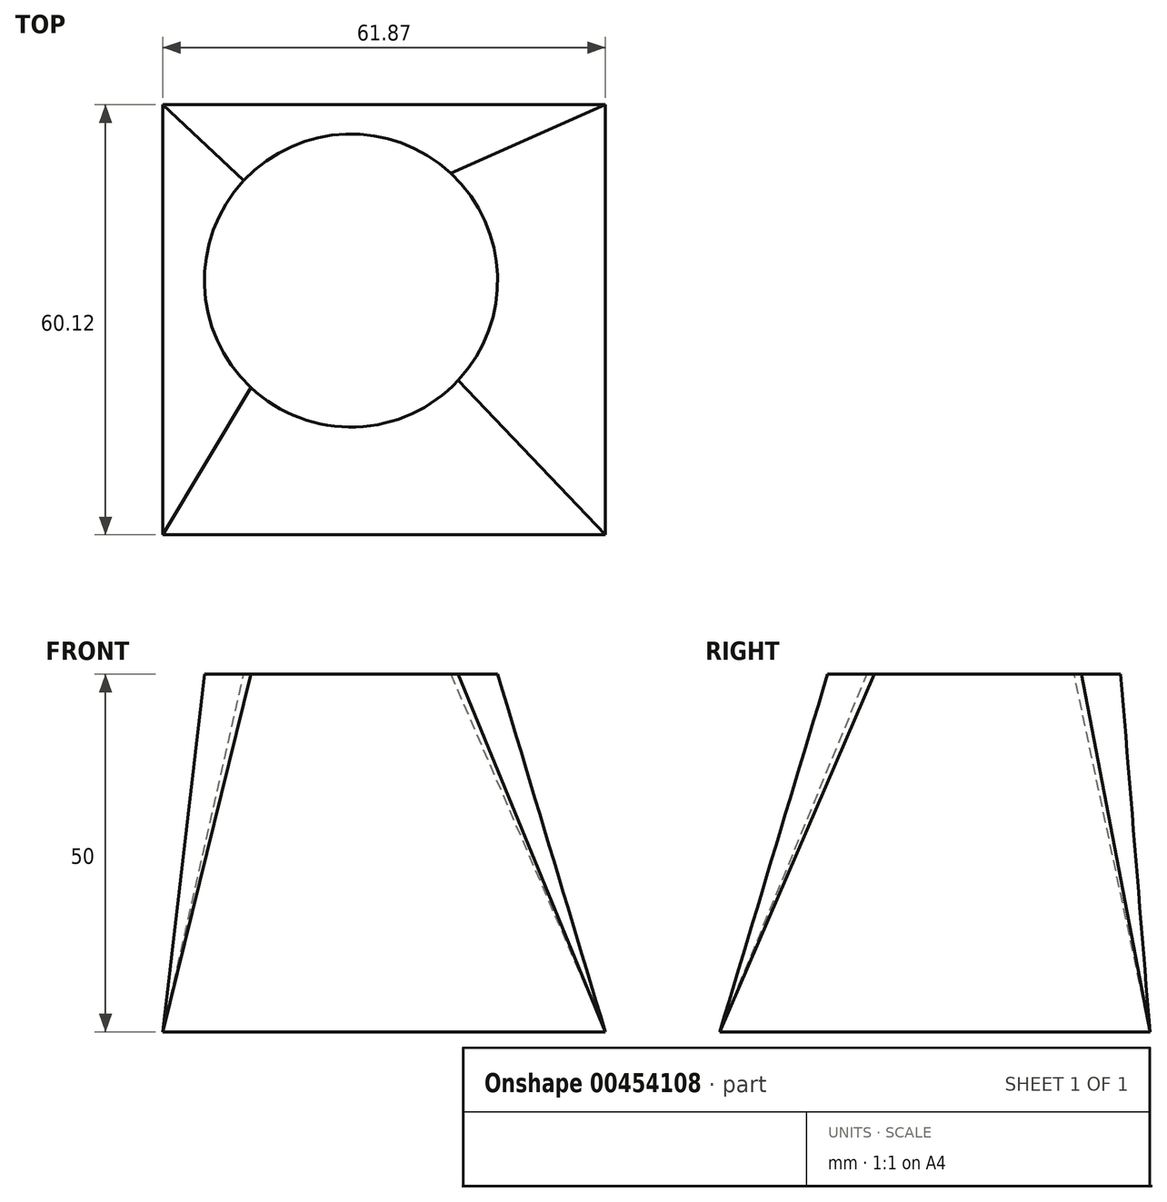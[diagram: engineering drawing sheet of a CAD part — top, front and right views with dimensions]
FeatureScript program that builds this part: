
annotation { "Feature Type Name" : "Feature", "Feature Type Description" : "" }
export const myFeature = defineFeature(function(context is Context, id is Id, definition is map)
    precondition{}
    {
        {
            var Q0;
            Q0=qCreatedBy(makeId("Top.planeOp"),FACE);
            var sketch = newSketch(context, id + "F0", { "sketchPlane" : qUnion([Q0])});
            skLineSegment(sketch, "E0.bottom", {"start": v(0, 0) * mm, "end": v(61.87, 0) * mm});
            skLineSegment(sketch, "E0.top", {"start": v(0, -60.12) * mm, "end": v(61.87, -60.12) * mm});
            skLineSegment(sketch, "E0.left", {"start": v(0, 0) * mm, "end": v(0, -60.12) * mm});
            skLineSegment(sketch, "E0.right", {"start": v(61.87, 0) * mm, "end": v(61.87, -60.12) * mm});
            skSolve(sketch);
        }
        {
            var Q0;
            Q0=qCreatedBy(makeId("Top.planeOp"),FACE);
            cPlane(context, id + "F1", {"entities" : qUnion([Q0]), "cplaneType" : CPlaneType.OFFSET, "offset" : 50 * mm, "width" : 150 * mm, "height" : 150 * mm});
        }
        {
            var Q0;
            Q0=qCreatedBy(id+"F1.planeOp",FACE);
            var sketch = newSketch(context, id + "F2", { "sketchPlane" : qUnion([Q0])});
            skCircle(sketch, "E1", {"center": v(26.33, -24.57) * mm, "radius": 20.49 * mm});
            skSolve(sketch);
        }
        {
            var Q0;
            Q0 = qSketchRegion(id + "F0", true);
            var Q1;
            Q1 = qSketchRegion(id + "F2", true);
            loft(context, id + "F3", {"sheetProfilesArray" : [{ "sheetProfileEntities" : qUnion([Q0]) }, { "sheetProfileEntities" : qUnion([Q1]) }]});
        }
    });
